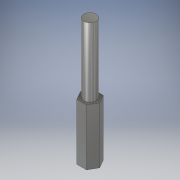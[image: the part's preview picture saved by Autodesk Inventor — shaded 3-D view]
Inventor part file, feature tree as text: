
AUTODESK INVENTOR PART (.ipt)
format: ipt  version: 2017 SP1 (Build 210196100, 196)  size: 112,640 bytes
history: native  units: in
note: dims shown in document units (in); Inventor stores cm internally (conversion verified against a paired STEP export)
features: extrude x3, sketch x3
ambient origin geometry x8: Origin, YZ Plane, XZ Plane, XY Plane, X Axis, Y Axis, Z Axis, Center Point
bodies: Solid1 (feature_tree)
feature tree (6):
  extrude  "Extrusion1"  Depth=1.6875in TaperAngle=0.0deg
  extrude  "Extrusion2"  Depth=2.0625in TaperAngle=0.0deg
  extrude  "Extrusion3"  Depth=1.0in TaperAngle=0.0deg
  sketch  "Sketch1"  dims[d0=0.5in d1=1.6875in d2=0.0in]
  sketch  "Sketch2"  dims[d3=0.375in d4=2.0625in d5=0.0in]
  sketch  "Sketch3"  dims[d7=0.15in d8=1.0in d9=0.0in]
